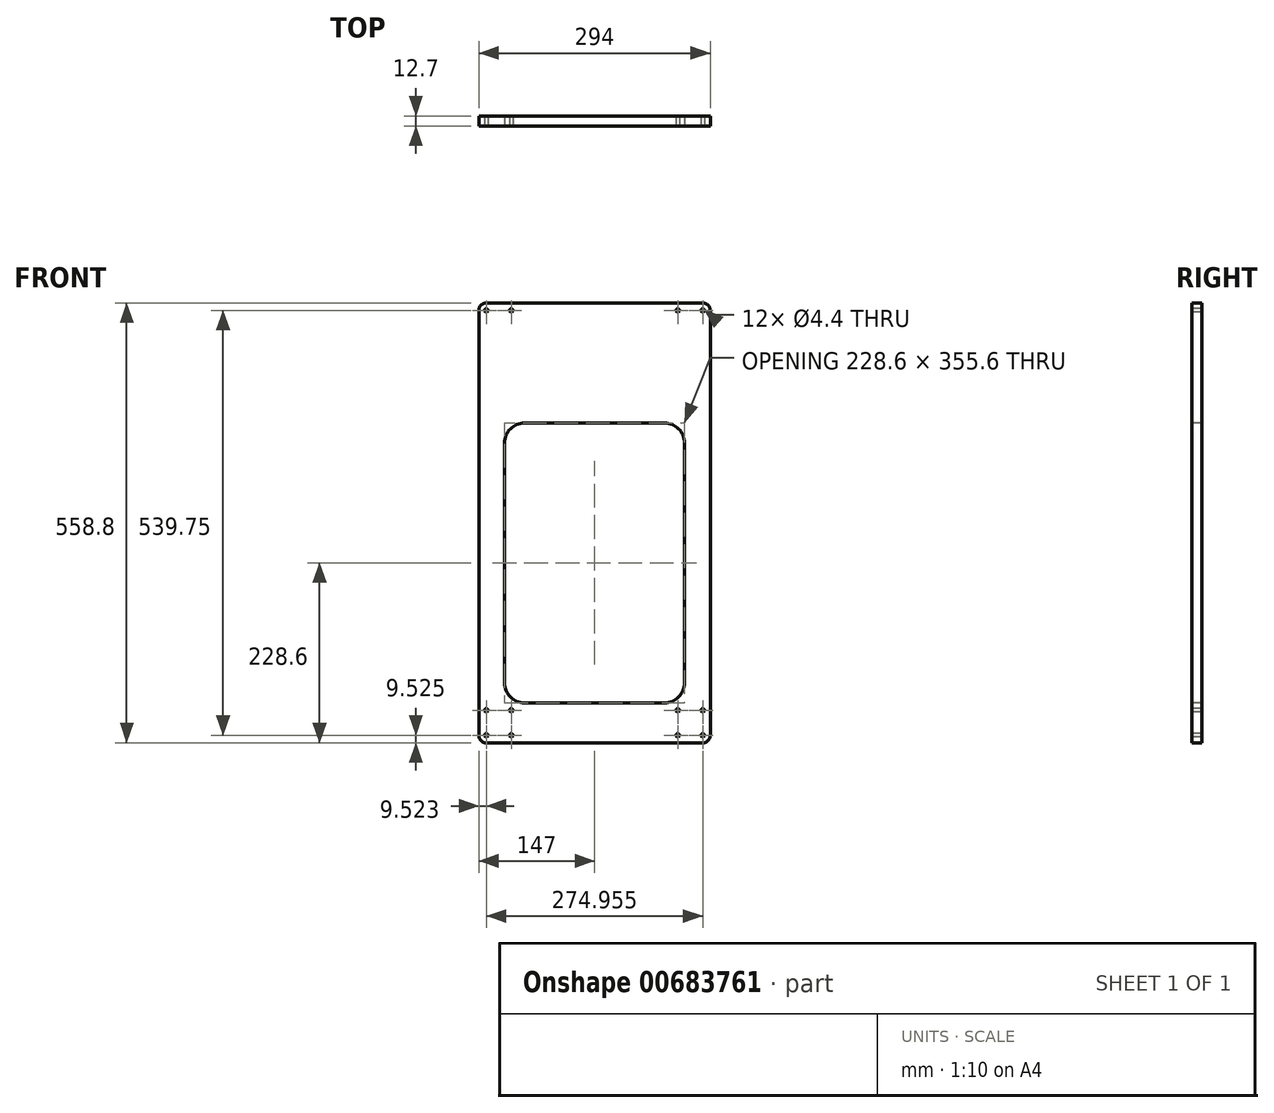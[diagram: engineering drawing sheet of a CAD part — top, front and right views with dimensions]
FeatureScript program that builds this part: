
annotation { "Feature Type Name" : "Feature", "Feature Type Description" : "" }
export const myFeature = defineFeature(function(context is Context, id is Id, definition is map)
    precondition{}
    {
        {
            var Q0;
            Q0=qCreatedBy(makeId("Front.planeOp"),FACE);
            var sketch = newSketch(context, id + "F0", { "sketchPlane" : qUnion([Q0])});
            skLineSegment(sketch, "E0.bottom", {"start": v(147, 279.4) * mm, "end": v(-147, 279.4) * mm});
            skLineSegment(sketch, "E0.top", {"start": v(147, -279.4) * mm, "end": v(-147, -279.4) * mm});
            skLineSegment(sketch, "E0.left", {"start": v(147, 279.4) * mm, "end": v(147, -279.4) * mm});
            skLineSegment(sketch, "E0.right", {"start": v(-147, 279.4) * mm, "end": v(-147, -279.4) * mm});
            skPoint(sketch, "E0.middle", {"position": v(0, 0) * mm});
            skSolve(sketch);
        }
        {
            var Q0;
            Q0=qSketchRegion(id+"F0",true);
            extrude(context, id + "F1", {"entities" : qUnion([Q0]), "depth" : 12.7 * mm, "offsetDistance" : 25.4 * mm});
        }
        {
            var Q0;
            Q0=makeQuery(id+"F1.opExtrude","CAP_FACE",FACE,{"disambiguationData":[OSD([sQuery(id+"F0.wireOp",EDGE,"E0.bottom"),sQuery(id+"F0.wireOp",EDGE,"E0.top"),sQuery(id+"F0.wireOp",EDGE,"E0.left"),sQuery(id+"F0.wireOp",EDGE,"E0.right")])],"isStart":false});
            var sketch = newSketch(context, id + "F2", { "sketchPlane" : qUnion([Q0])});
            skLineSegment(sketch, "E1", {"start": v(0, -279.4) * mm, "end": v(0, 0) * mm, "construction": true});
            skLineSegment(sketch, "E2", {"start": v(-147, -254) * mm, "end": v(147, -254) * mm, "construction": true});
            skLineSegment(sketch, "E3", {"start": v(-121.6, -254) * mm, "end": v(-121.6, -279.4) * mm, "construction": true});
            skPoint(sketch, "E4", {"position": v(-137.48, -238.13) * mm});
            skPoint(sketch, "E5.MirrorP", {"position": v(-137.48, -269.88) * mm});
            skPoint(sketch, "E6.MirrorP", {"position": v(-105.73, -269.88) * mm});
            skPoint(sketch, "E7.MirrorP", {"position": v(-105.73, -238.13) * mm});
            skPoint(sketch, "E8.MirrorP", {"position": v(137.48, -269.88) * mm});
            skPoint(sketch, "E9.MirrorP", {"position": v(137.48, -238.13) * mm});
            skPoint(sketch, "E10.MirrorP", {"position": v(105.73, -238.13) * mm});
            skPoint(sketch, "E11.MirrorP", {"position": v(105.73, -269.88) * mm});
            skLineSegment(sketch, "E12", {"start": v(0, 0) * mm, "end": v(147, 0) * mm, "construction": true});
            skPoint(sketch, "E13.MirrorP", {"position": v(137.48, 269.88) * mm});
            skPoint(sketch, "E14.MirrorP", {"position": v(105.73, 269.88) * mm});
            skPoint(sketch, "E15.MirrorP", {"position": v(-105.73, 269.88) * mm});
            skPoint(sketch, "E16.MirrorP", {"position": v(-137.48, 269.88) * mm});
            skSolve(sketch);
        }
        {
            var Q0;
            Q0=sQuery(id+"F2.wireOp",VERTEX,"E16.MirrorP");
            var Q1;
            Q1=sQuery(id+"F2.wireOp",VERTEX,"E15.MirrorP");
            var Q2;
            Q2=sQuery(id+"F2.wireOp",VERTEX,"E14.MirrorP");
            var Q3;
            Q3=sQuery(id+"F2.wireOp",VERTEX,"E13.MirrorP");
            var Q4;
            Q4=sQuery(id+"F2.wireOp",VERTEX,"E10.MirrorP");
            var Q5;
            Q5=sQuery(id+"F2.wireOp",VERTEX,"E9.MirrorP");
            var Q6;
            Q6=sQuery(id+"F2.wireOp",VERTEX,"E8.MirrorP");
            var Q7;
            Q7=sQuery(id+"F2.wireOp",VERTEX,"E11.MirrorP");
            var Q8;
            Q8=sQuery(id+"F2.wireOp",VERTEX,"E6.MirrorP");
            var Q9;
            Q9=sQuery(id+"F2.wireOp",VERTEX,"E5.MirrorP");
            var Q10;
            Q10=sQuery(id+"F2.wireOp",VERTEX,"E4");
            var Q11;
            Q11=sQuery(id+"F2.wireOp",VERTEX,"E7.MirrorP");
            var Q12;
            Q12=makeQuery(id+"F1.opExtrude","SWEPT_BODY",BODY,{"disambiguationData":[OSD([sQuery(id+"F0.wireOp",EDGE,"E0.bottom"),sQuery(id+"F0.wireOp",EDGE,"E0.top"),sQuery(id+"F0.wireOp",EDGE,"E0.left"),sQuery(id+"F0.wireOp",EDGE,"E0.right")])]});
            hole(context, id + "F3", {"style" : HoleStyle.SIMPLE, "endStyle" : HoleEndStyle.THROUGH, "standardTappedOrClearance" : lookupTablePath({ "standard" : "ISO", "fit" : "Normal", "size" : "M4", "type" : "Clearance" }), "standardBlindInLast" : lookupTablePath({ "fit" : "Standard", "standard" : "ISO", "size" : "M4", "type" : "Clearance" }), "holeDiameter" : 4.4 * mm, "majorDiameter" : 6.35 * mm, "isTappedThrough" : true, "tappedDepth" : 12.7 * mm, "tapClearance" : 3, "locations" : qUnion([Q0, Q1, Q2, Q3, Q4, Q5, Q6, Q7, Q8, Q9, Q10, Q11]), "scope" : qUnion([Q12])});
        }
        {
            var Q0;
            Q0=makeQuery(id+"F1.opExtrude","SWEPT_EDGE",EDGE,{"disambiguationData":[OSD([sQuery(id+"F0.wireOp",EDGE,"E0.bottom"),sQuery(id+"F0.wireOp",EDGE,"E0.left")])]});
            var Q1;
            Q1=makeQuery(id+"F1.opExtrude","SWEPT_EDGE",EDGE,{"disambiguationData":[OSD([sQuery(id+"F0.wireOp",EDGE,"E0.top"),sQuery(id+"F0.wireOp",EDGE,"E0.left")])]});
            var Q2;
            Q2=makeQuery(id+"F1.opExtrude","SWEPT_EDGE",EDGE,{"disambiguationData":[OSD([sQuery(id+"F0.wireOp",EDGE,"E0.top"),sQuery(id+"F0.wireOp",EDGE,"E0.right")])]});
            var Q3;
            Q3=makeQuery(id+"F1.opExtrude","SWEPT_EDGE",EDGE,{"disambiguationData":[OSD([sQuery(id+"F0.wireOp",EDGE,"E0.bottom"),sQuery(id+"F0.wireOp",EDGE,"E0.right")])]});
            fillet(context, id + "F4", {"entities" : qUnion([Q0, Q1, Q2, Q3]), "radius" : 9.52 * mm, "tangentPropagation" : true, "allowEdgeOverflow" : false});
        }
        {
            var Q0;
            Q0=makeQuery(id+"F1.opExtrude","CAP_FACE",FACE,{"disambiguationData":[OSD([sQuery(id+"F0.wireOp",EDGE,"E0.bottom"),sQuery(id+"F0.wireOp",EDGE,"E0.top"),sQuery(id+"F0.wireOp",EDGE,"E0.left"),sQuery(id+"F0.wireOp",EDGE,"E0.right")])],"isStart":false});
            var sketch = newSketch(context, id + "F5", { "sketchPlane" : qUnion([Q0])});
            skLineSegment(sketch, "E17.bottom", {"start": v(-88.9, 127) * mm, "end": v(88.9, 127) * mm});
            skLineSegment(sketch, "E17.top", {"start": v(-88.9, -228.6) * mm, "end": v(88.9, -228.6) * mm});
            skLineSegment(sketch, "E17.left", {"start": v(-114.3, 101.6) * mm, "end": v(-114.3, -203.2) * mm});
            skLineSegment(sketch, "E17.right", {"start": v(114.3, 101.6) * mm, "end": v(114.3, -203.2) * mm});
            skLineSegment(sketch, "E18", {"start": v(0, 0) * mm, "end": v(0, 127) * mm, "construction": true});
            skPoint(sketch, "E19.visualSharp", {"position": v(-114.3, 127) * mm});
            skArc(sketch, "E19.filletArc", {"start": v(-88.9, 127) * mm, "mid": v(-106.86, 119.56) * mm, "end": v(-114.3, 101.6) * mm});
            skPoint(sketch, "E20.visualSharp", {"position": v(114.3, 127) * mm});
            skArc(sketch, "E20.filletArc", {"start": v(114.3, 101.6) * mm, "mid": v(106.86, 119.56) * mm, "end": v(88.9, 127) * mm});
            skPoint(sketch, "E21.visualSharp", {"position": v(114.3, -228.6) * mm});
            skArc(sketch, "E21.filletArc", {"start": v(88.9, -228.6) * mm, "mid": v(106.86, -221.16) * mm, "end": v(114.3, -203.2) * mm});
            skPoint(sketch, "E22.visualSharp", {"position": v(-114.3, -228.6) * mm});
            skArc(sketch, "E22.filletArc", {"start": v(-114.3, -203.2) * mm, "mid": v(-106.86, -221.16) * mm, "end": v(-88.9, -228.6) * mm});
            skSolve(sketch);
        }
        {
            var Q0;
            Q0=qSketchRegion(id+"F5",true);
            extrude(context, id + "F6", {"entities" : qUnion([Q0]), "operationType" : NewBodyOperationType.REMOVE, "endBound" : BoundingType.THROUGH_ALL, "oppositeDirection" : true, "depth" : 25.4 * mm, "offsetDistance" : 25.4 * mm});
        }
    });
